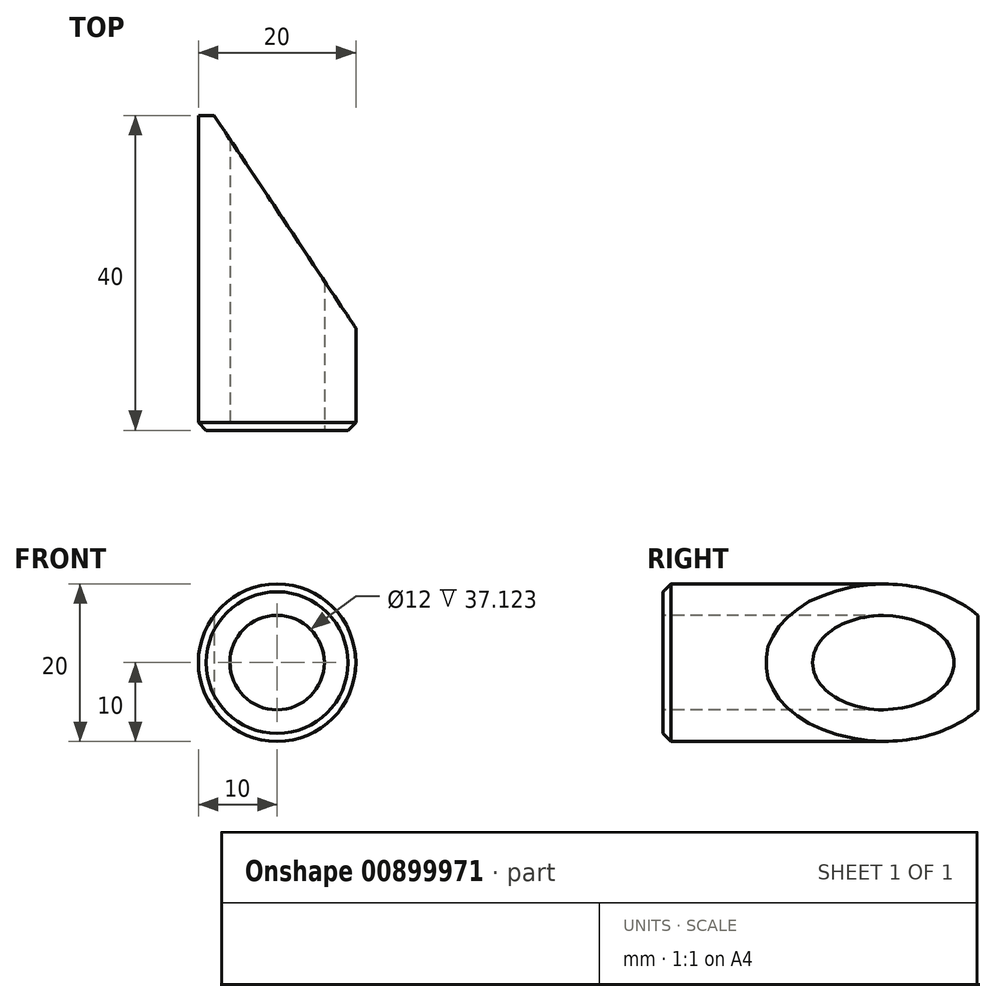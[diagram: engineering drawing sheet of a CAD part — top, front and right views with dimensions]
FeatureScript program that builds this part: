
annotation { "Feature Type Name" : "Feature", "Feature Type Description" : "" }
export const myFeature = defineFeature(function(context is Context, id is Id, definition is map)
    precondition{}
    {
        {
            var Q0;
            Q0=qCreatedBy(makeId("Top.planeOp"),FACE);
            var sketch = newSketch(context, id + "F0", { "sketchPlane" : qUnion([Q0])});
            skLineSegment(sketch, "E0", {"start": v(0, 0) * mm, "end": v(10, 0) * mm});
            skLineSegment(sketch, "E1", {"start": v(10, 0) * mm, "end": v(10, 40) * mm});
            skLineSegment(sketch, "E2", {"start": v(10, 40) * mm, "end": v(0, 40) * mm});
            skLineSegment(sketch, "E3", {"start": v(0, 40) * mm, "end": v(0, 0) * mm});
            skSolve(sketch);
        }
        {
            var Q0;
            Q0=makeQuery(id+"F0.imprint","IMPRINT",FACE,{"disambiguationData":[TD([[makeQuery(id+"F0.imprint","IMPRINT",EDGE,{"derivedFrom":sQuery(id+"F0.wireOp",EDGE,"E0")}),1.0]])]});
            var Q1;
            Q1=sQuery(id+"F0.wireOp",EDGE,"E3");
            revolve(context, id + "F1", {"surfaceOperationType" : NewSurfaceOperationType.NEW, "entities" : qUnion([Q0]), "axis" : qUnion([Q1]), "revolveType" : RevolveType.FULL});
        }
        {
            var Q0;
            Q0=qCreatedBy(makeId("Top.planeOp"),FACE);
            var sketch = newSketch(context, id + "F2", { "sketchPlane" : qUnion([Q0])});
            skLineSegment(sketch, "E4.0", {"start": v(-8, 40) * mm, "end": v(10, 40) * mm});
            skLineSegment(sketch, "E5.0", {"start": v(10, 13) * mm, "end": v(10, 40) * mm});
            skLineSegment(sketch, "E6", {"start": v(10, 13) * mm, "end": v(-8, 40) * mm});
            skSolve(sketch);
        }
        {
            var Q0;
            Q0=makeQuery(id+"F2.imprint","IMPRINT",FACE,{"disambiguationData":[TD([[makeQuery(id+"F2.imprint","IMPRINT",EDGE,{"derivedFrom":sQuery(id+"F2.wireOp",EDGE,"E4.0")}),-1.0]])]});
            extrude(context, id + "F3", {"entities" : qUnion([Q0]), "operationType" : NewBodyOperationType.REMOVE, "endBound" : BoundingType.SYMMETRIC, "depth" : 50 * mm, "offsetDistance" : 25 * mm});
        }
        {
            var Q0;
            Q0=makeQuery(id+"F1.opRevolve","SWEPT_EDGE",EDGE,{"disambiguationData":[OSD([sQuery(id+"F0.wireOp",EDGE,"E0"),sQuery(id+"F0.wireOp",EDGE,"E1")])]});
            chamfer(context, id + "F4", {"entities" : qUnion([Q0]), "width" : 1 * mm, "tangentPropagation" : true});
        }
        {
            var Q0;
            Q0=makeQuery(id+"F1.opRevolve","SWEPT_FACE",FACE,{"disambiguationData":[OSD([sQuery(id+"F0.wireOp",EDGE,"E0")])]});
            var sketch = newSketch(context, id + "F5", { "sketchPlane" : qUnion([Q0])});
            skCircle(sketch, "E7", {"center": v(0, 0) * mm, "radius": 6 * mm});
            skSolve(sketch);
        }
        {
            var Q0;
            Q0=makeQuery(id+"F5.imprint","IMPRINT",FACE,{"disambiguationData":[TD([[makeQuery(id+"F5.imprint","IMPRINT",EDGE,{"derivedFrom":sQuery(id+"F5.wireOp",EDGE,"E7")}),1.0]])]});
            extrude(context, id + "F6", {"entities" : qUnion([Q0]), "operationType" : NewBodyOperationType.REMOVE, "oppositeDirection" : true, "depth" : 50 * mm, "offsetDistance" : 25 * mm});
        }
    });
